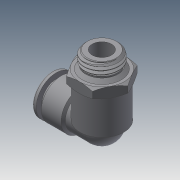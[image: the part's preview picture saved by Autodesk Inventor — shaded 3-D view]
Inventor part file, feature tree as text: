
AUTODESK INVENTOR PART (.ipt)
format: ipt  version: 2020.3 (Build 243373000, 373)  size: 423,424 bytes
history: native  units: in
note: dims shown in document units (in); Inventor stores cm internally (conversion verified against a paired STEP export)
features: revolve x1, other x1
ambient origin geometry x8: Origin, YZ Plane, XZ Plane, XY Plane, X Axis, Y Axis, Z Axis, Center Point
bodies: Solid1 (feature_tree), Solid2 (feature_tree)
feature tree (2):
  revolve  "Revolve4"  [1 undecoded]
  other  "Cut-Sweep4"
note: 1 required parameter value undecoded (feature->parameter linkage not recoverable at this tier; creation-order binding heuristic only, values carry confidence <= 0.55)
